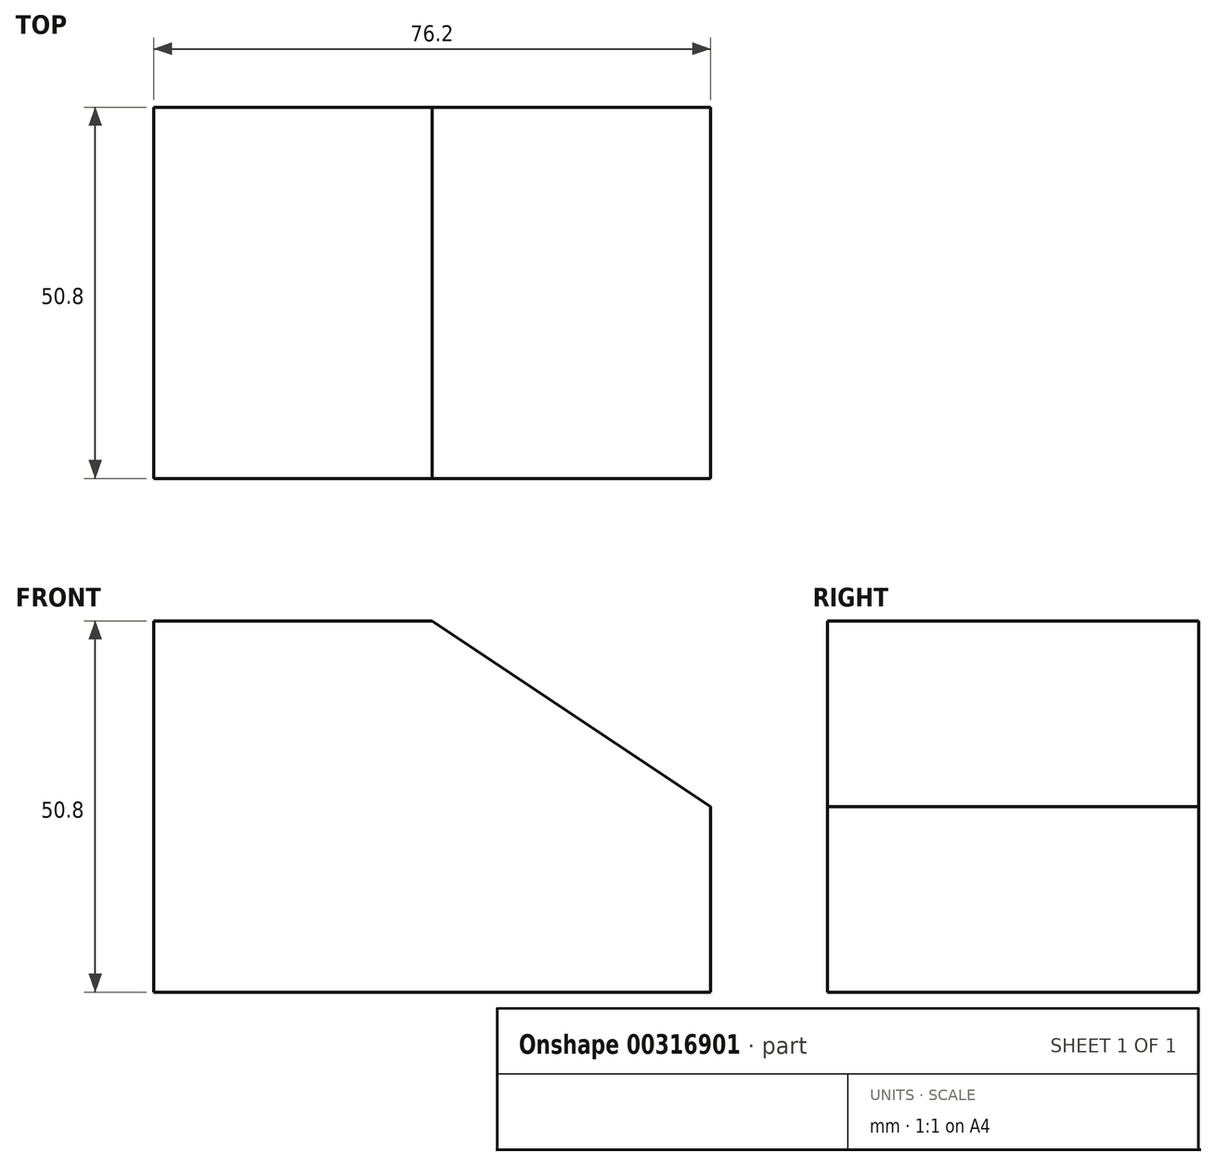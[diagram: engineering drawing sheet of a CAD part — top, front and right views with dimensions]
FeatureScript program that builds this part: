
annotation { "Feature Type Name" : "Feature", "Feature Type Description" : "" }
export const myFeature = defineFeature(function(context is Context, id is Id, definition is map)
    precondition{}
    {
        {
            var Q0;
            Q0=qCreatedBy(makeId("Front.planeOp"),FACE);
            var sketch = newSketch(context, id + "F0", { "sketchPlane" : qUnion([Q0])});
            skLineSegment(sketch, "E0", {"start": v(21.64, -14.21) * mm, "end": v(-54.56, -14.21) * mm});
            skLineSegment(sketch, "E1", {"start": v(-54.56, -14.21) * mm, "end": v(-54.56, 36.59) * mm});
            skLineSegment(sketch, "E2", {"start": v(-54.56, 36.59) * mm, "end": v(-16.46, 36.59) * mm});
            skLineSegment(sketch, "E3", {"start": v(21.64, -14.21) * mm, "end": v(21.64, 11.19) * mm});
            skLineSegment(sketch, "E4", {"start": v(21.64, 11.19) * mm, "end": v(-16.46, 36.59) * mm});
            skSolve(sketch);
        }
        {
            var Q0;
            Q0=makeQuery(id+"F0.imprint","IMPRINT",FACE,{"disambiguationData":[TD([[makeQuery(id+"F0.imprint","IMPRINT",EDGE,{"derivedFrom":sQuery(id+"F0.wireOp",EDGE,"E0")}),-1.0]])]});
            extrude(context, id + "F1", {"entities" : qUnion([Q0]), "depth" : 50.8 * mm});
        }
    });
